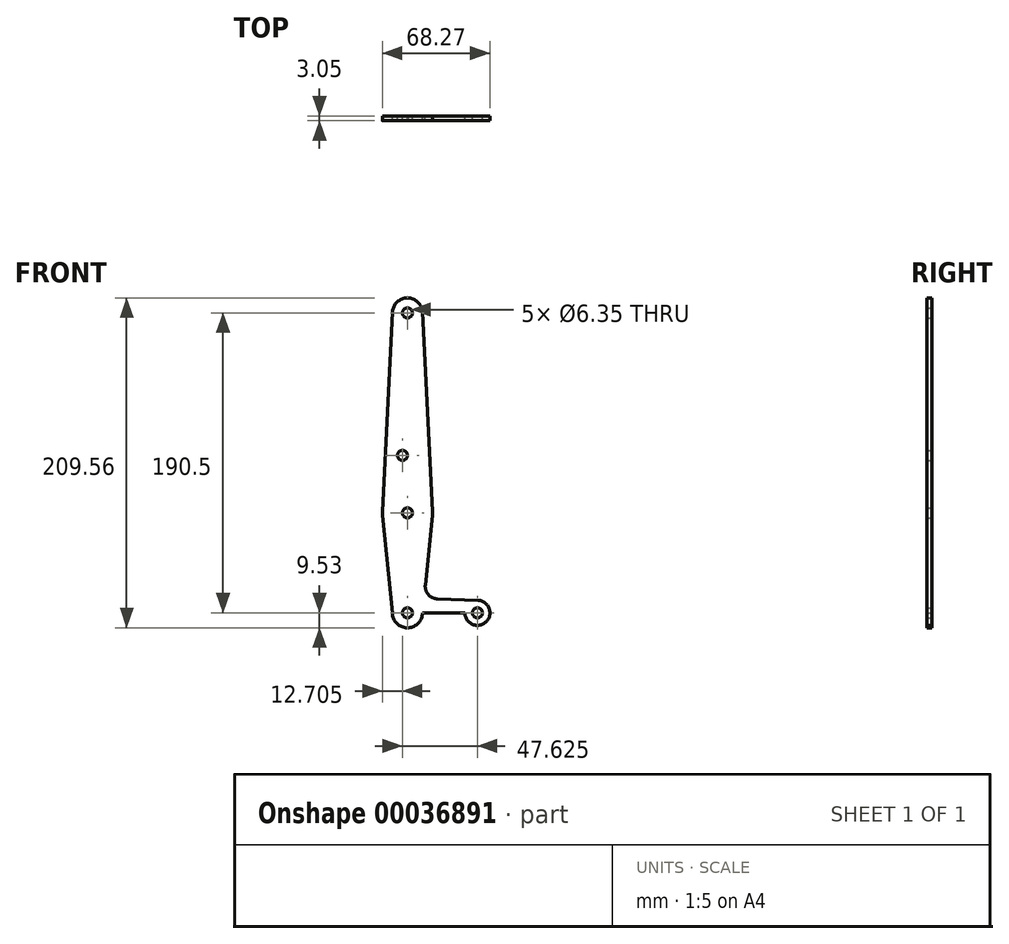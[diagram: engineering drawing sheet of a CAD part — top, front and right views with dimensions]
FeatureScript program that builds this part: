
annotation { "Feature Type Name" : "Feature", "Feature Type Description" : "" }
export const myFeature = defineFeature(function(context is Context, id is Id, definition is map)
    precondition{}
    {
        {
            var Q0;
            Q0=qCreatedBy(makeId("Front.planeOp"),FACE);
            var sketch = newSketch(context, id + "F0", { "sketchPlane" : qUnion([Q0])});
            skCircle(sketch, "E0", {"center": v(0, 0) * mm, "radius": 9.53 * mm});
            skCircle(sketch, "E1", {"center": v(0, 63.5) * mm, "radius": 15.88 * mm});
            skCircle(sketch, "E2", {"center": v(0, 190.5) * mm, "radius": 9.53 * mm});
            skCircle(sketch, "E3", {"center": v(44.45, 0) * mm, "radius": 7.94 * mm});
            skLineSegment(sketch, "E4", {"start": v(0, 190.5) * mm, "end": v(0, 0) * mm});
            skLineSegment(sketch, "E5", {"start": v(0, 0) * mm, "end": v(44.45, 0) * mm});
            skLineSegment(sketch, "E6", {"start": v(18.97, 8.85) * mm, "end": v(44.73, 7.93) * mm});
            skLineSegment(sketch, "E7", {"start": v(0, -9.53) * mm, "end": v(44.73, -7.93) * mm});
            skLineSegment(sketch, "E8", {"start": v(-9.51, 190.98) * mm, "end": v(-15.86, 64.3) * mm});
            skLineSegment(sketch, "E9", {"start": v(-9.52, 0) * mm, "end": v(-15.8, 61.9) * mm});
            skLineSegment(sketch, "E10", {"start": v(9.51, 190.98) * mm, "end": v(15.86, 64.3) * mm});
            skLineSegment(sketch, "E11", {"start": v(15.8, 61.91) * mm, "end": v(11.34, 17.59) * mm});
            skCircle(sketch, "E12", {"center": v(0, 190.5) * mm, "radius": 3.18 * mm});
            skCircle(sketch, "E13", {"center": v(0, 63.5) * mm, "radius": 3.18 * mm});
            skCircle(sketch, "E14", {"center": v(0, 0) * mm, "radius": 3.18 * mm});
            skCircle(sketch, "E15", {"center": v(44.45, 0) * mm, "radius": 3.18 * mm});
            skCircle(sketch, "E16", {"center": v(-3.17, 100.03) * mm, "radius": 3.18 * mm});
            skPoint(sketch, "E17.newPointB", {"position": v(0, 9.52) * mm});
            skArc(sketch, "E17.filletArc", {"start": v(11.34, 17.59) * mm, "mid": v(13.26, 11.57) * mm, "end": v(18.97, 8.85) * mm});
            skSolve(sketch);
        }
        {
            var Q0;
            Q0=makeQuery(id+"F0.imprint","IMPRINT",FACE,{"disambiguationData":[TD([[makeQuery(id+"F0.imprint","IMPRINT",EDGE,{"derivedFrom":sQuery(id+"F0.wireOp",EDGE,"E12")}),-1.0]])]});
            var Q1;
            {var subQ4=sQuery(id+"F0.wireOp",EDGE,"E8");Q1=makeQuery(id+"F0.imprint","IMPRINT",FACE,{"disambiguationData":[TD([[makeQuery(id+"F0.imprint","IMPRINT",EDGE,{"derivedFrom":subQ4}),1.0]])]});}
            var Q2;
            {var subQ0=sQuery(id+"F0.wireOp",EDGE,"E10");Q2=makeQuery(id+"F0.imprint","IMPRINT",FACE,{"disambiguationData":[TD([[makeQuery(id+"F0.imprint","IMPRINT",EDGE,{"derivedFrom":subQ0}),-1.0]])]});}
            var Q3;
            {var subQ4=sQuery(id+"F0.wireOp",EDGE,"E1");var subQ7=makeQuery(id+"F0.imprint","INTERSECT",VERTEX,{"derivedFrom":[subQ4,sQuery(id+"F0.wireOp",EDGE,"E10")]});Q3=makeQuery(id+"F0.imprint","IMPRINT",FACE,{"disambiguationData":[TD([[makeQuery(id+"F0.imprint","IMPRINT",EDGE,{"disambiguationData":[TD([[subQ7,-1.0]])],"derivedFrom":subQ4}),1.0]])]});}
            var Q4;
            {var subQ4=sQuery(id+"F0.wireOp",EDGE,"E1");var subQ6=makeQuery(id+"F0.imprint","INTERSECT",VERTEX,{"derivedFrom":[subQ4,sQuery(id+"F0.wireOp",EDGE,"E8")]});Q4=makeQuery(id+"F0.imprint","IMPRINT",FACE,{"disambiguationData":[TD([[makeQuery(id+"F0.imprint","IMPRINT",EDGE,{"disambiguationData":[TD([[subQ6,1.0]])],"derivedFrom":subQ4}),1.0]])]});}
            var Q5;
            {var subQ5=sQuery(id+"F0.wireOp",EDGE,"E9");Q5=makeQuery(id+"F0.imprint","IMPRINT",FACE,{"disambiguationData":[TD([[makeQuery(id+"F0.imprint","IMPRINT",EDGE,{"derivedFrom":subQ5}),-1.0]])]});}
            var Q6;
            {var subQ1=sQuery(id+"F0.wireOp",EDGE,"E6");Q6=makeQuery(id+"F0.imprint","IMPRINT",FACE,{"disambiguationData":[TD([[makeQuery(id+"F0.imprint","IMPRINT",EDGE,{"derivedFrom":subQ1}),-1.0]])]});}
            var Q7;
            Q7=makeQuery(id+"F0.imprint","IMPRINT",FACE,{"disambiguationData":[TD([[makeQuery(id+"F0.imprint","IMPRINT",EDGE,{"derivedFrom":sQuery(id+"F0.wireOp",EDGE,"E15")}),-1.0]])]});
            var Q8;
            {var subQ5=sQuery(id+"F0.wireOp",EDGE,"E0");var subQ8=makeQuery(id+"F0.imprint","INTERSECT",VERTEX,{"derivedFrom":[subQ5,sQuery(id+"F0.wireOp",EDGE,"E9")]});Q8=makeQuery(id+"F0.imprint","IMPRINT",FACE,{"disambiguationData":[TD([[makeQuery(id+"F0.imprint","IMPRINT",EDGE,{"disambiguationData":[TD([[subQ8,1.0]])],"derivedFrom":subQ5}),1.0]])]});}
            var Q9;
            {var subQ3=sQuery(id+"F0.wireOp",EDGE,"E0");var subQ5=sQuery(id+"F0.wireOp",EDGE,"E4");var subQ7=makeQuery(id+"F0.imprint","INTERSECT",VERTEX,{"derivedFrom":[subQ3,subQ5]});Q9=makeQuery(id+"F0.imprint","IMPRINT",FACE,{"disambiguationData":[TD([[makeQuery(id+"F0.imprint","IMPRINT",EDGE,{"disambiguationData":[TD([[subQ7,1.0]])],"derivedFrom":subQ3}),1.0]])]});}
            var Q10;
            {var subQ0=sQuery(id+"F0.wireOp",EDGE,"E7");var subQ1=sQuery(id+"F0.wireOp",EDGE,"E0");var subQ2=makeQuery(id+"F0.imprint","INTERSECT",VERTEX,{"disambiguationData":[OD(1.0)],"derivedFrom":[subQ1,subQ0]});Q10=makeQuery(id+"F0.imprint","IMPRINT",FACE,{"disambiguationData":[TD([[makeQuery(id+"F0.imprint","IMPRINT",EDGE,{"disambiguationData":[TD([[subQ2,-1.0]])],"derivedFrom":subQ1}),-1.0]])]});}
            extrude(context, id + "F1", {"entities" : qUnion([Q0, Q1, Q2, Q3, Q4, Q5, Q6, Q7, Q8, Q9, Q10]), "depth" : 3.05 * mm});
        }
    });
